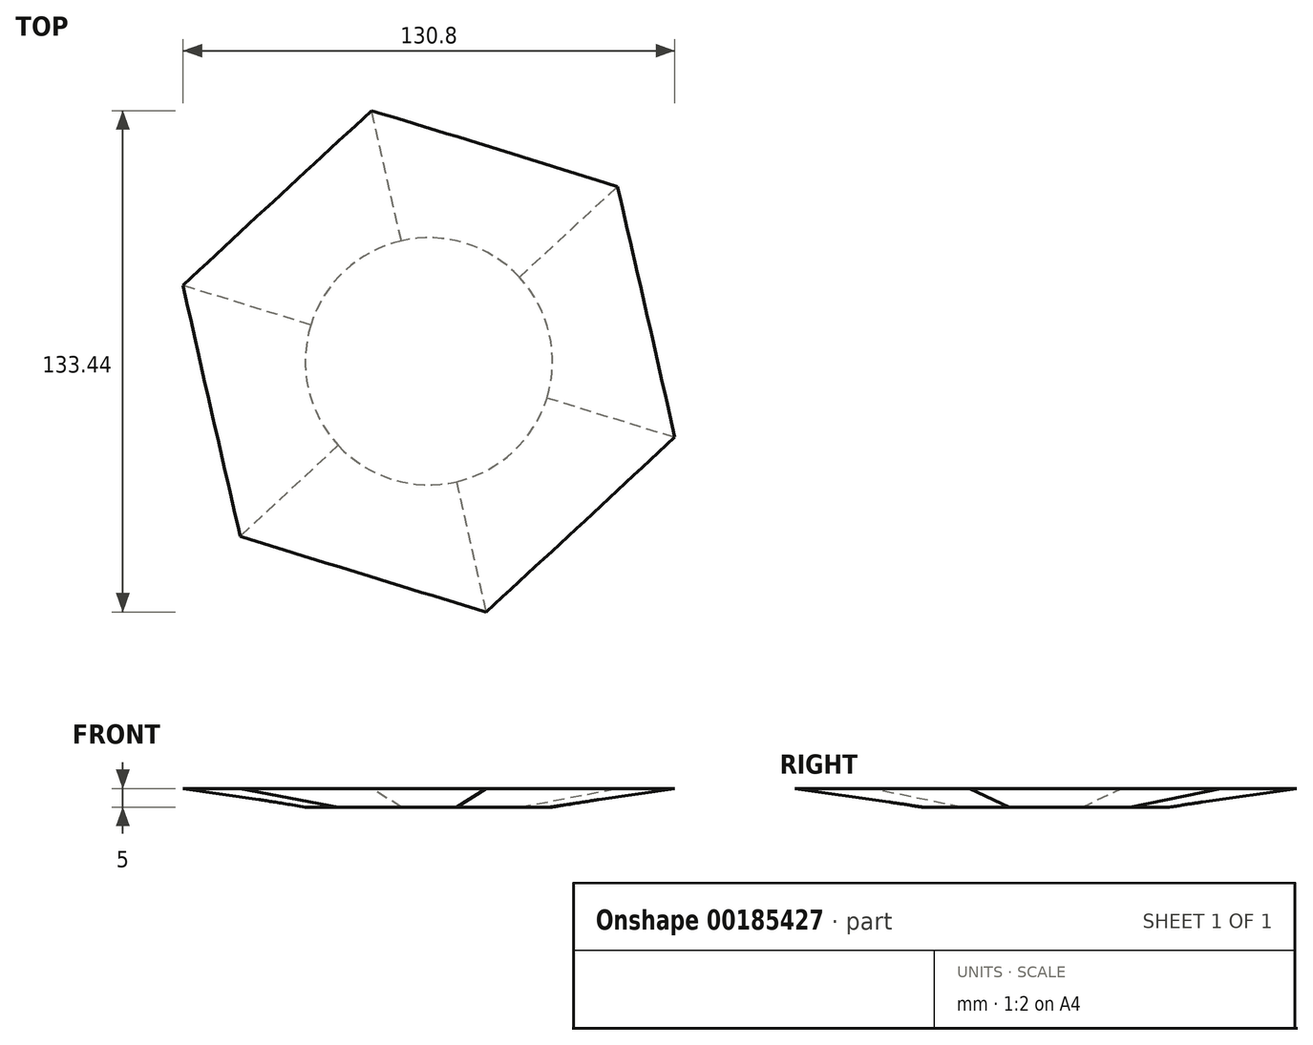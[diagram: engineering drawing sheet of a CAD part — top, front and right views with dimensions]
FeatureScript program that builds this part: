
annotation { "Feature Type Name" : "Feature", "Feature Type Description" : "" }
export const myFeature = defineFeature(function(context is Context, id is Id, definition is map)
    precondition{}
    {
        {
            assignVariable(context, id + "F0", {"name" : "vaseThickness", "anyValue" : 0.1});
        }
        {
            assignVariable(context, id + "F1", {"name" : "vaseHeight", "anyValue" : 5});
        }
        {
            var Q0;
            Q0=qCreatedBy(makeId("Top.planeOp"),FACE);
            var sketch = newSketch(context, id + "F2", { "sketchPlane" : qUnion([Q0])});
            skCircle(sketch, "E0", {"center": v(0, 0) * mm, "radius": 32.88 * mm});
            skSolve(sketch);
        }
        {
            var Q0;
            Q0=makeQuery(id+"F2.imprint","IMPRINT",FACE,{"disambiguationData":[TD([[makeQuery(id+"F2.imprint","IMPRINT",EDGE,{"derivedFrom":sQuery(id+"F2.wireOp",EDGE,"E0")}),1.0]])]});
            cPlane(context, id + "F3", {"entities" : qUnion([Q0]), "cplaneType" : CPlaneType.OFFSET, "offset" : (getVariable(context, 'vaseHeight') + getVariable(context, 'vaseThickness')) * mm, "width" : 152.4 * mm, "height" : 152.4 * mm});
        }
        {
            var Q0;
            Q0=qCreatedBy(id+"F3.planeOp",FACE);
            var sketch = newSketch(context, id + "F4", { "sketchPlane" : qUnion([Q0])});
            skCircle(sketch, "E1.cCircle", {"center": v(0, 0) * mm, "radius": 59.89 * mm, "construction": true});
            skLineSegment(sketch, "E1.0", {"start": v(-66.08, 20.4) * mm, "end": v(-15.38, 67.42) * mm});
            skLineSegment(sketch, "E1.1", {"start": v(-15.38, 67.42) * mm, "end": v(50.7, 47.03) * mm});
            skLineSegment(sketch, "E1.2", {"start": v(50.7, 47.03) * mm, "end": v(66.08, -20.4) * mm});
            skLineSegment(sketch, "E1.3", {"start": v(66.08, -20.4) * mm, "end": v(15.38, -67.42) * mm});
            skLineSegment(sketch, "E1.4", {"start": v(15.38, -67.42) * mm, "end": v(-50.7, -47.03) * mm});
            skLineSegment(sketch, "E1.5", {"start": v(-50.7, -47.03) * mm, "end": v(-66.08, 20.4) * mm});
            skPoint(sketch, "E1.0.midPoint", {"position": v(-40.73, 43.9) * mm});
            skSolve(sketch);
        }
        {
            var Q0;
            Q0=makeQuery(id+"F2.imprint","IMPRINT",FACE,{"disambiguationData":[TD([[makeQuery(id+"F2.imprint","IMPRINT",EDGE,{"derivedFrom":sQuery(id+"F2.wireOp",EDGE,"E0")}),1.0]])]});
            var Q1;
            Q1=makeQuery(id+"F4.imprint","IMPRINT",FACE,{"disambiguationData":[TD([[makeQuery(id+"F4.imprint","IMPRINT",EDGE,{"derivedFrom":sQuery(id+"F4.wireOp",EDGE,"E1.0")}),-1.0]])]});
            loft(context, id + "F5", {"sheetProfilesArray" : [{ "sheetProfileEntities" : qUnion([Q0]) }, { "sheetProfileEntities" : qUnion([Q1]) }]});
        }
        {
            var Q0;
            Q0=makeQuery(id+"F5.opLoft","CAP_FACE",FACE,{"disambiguationData":[OSD([makeQuery(id+"F4.imprint","IMPRINT",FACE,{"disambiguationData":[TD([[makeQuery(id+"F4.imprint","IMPRINT",EDGE,{"derivedFrom":sQuery(id+"F4.wireOp",EDGE,"E1.0")}),-1.0]])]})])],"isStart":true});
            extrude(context, id + "F6", {"entities" : qUnion([Q0]), "operationType" : NewBodyOperationType.REMOVE, "oppositeDirection" : true, "depth" : (getVariable(context, 'vaseThickness')) * mm});
        }
    });
